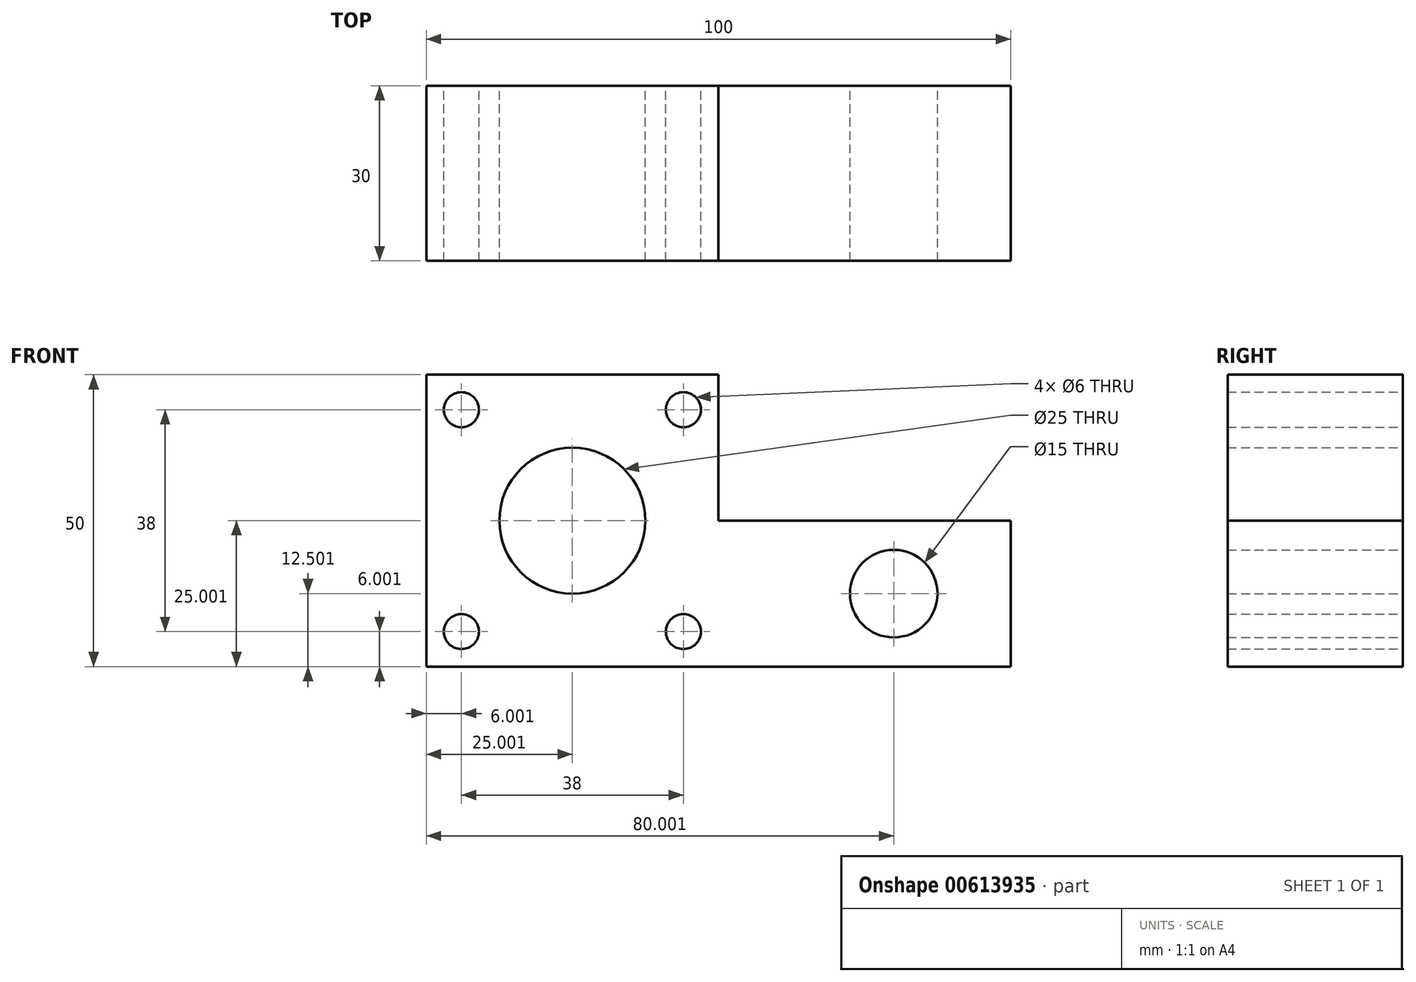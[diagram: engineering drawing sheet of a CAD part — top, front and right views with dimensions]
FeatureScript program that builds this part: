
annotation { "Feature Type Name" : "Feature", "Feature Type Description" : "" }
export const myFeature = defineFeature(function(context is Context, id is Id, definition is map)
    precondition{}
    {
        {
            var Q0;
            Q0=qCreatedBy(makeId("Front.planeOp"),FACE);
            var sketch = newSketch(context, id + "F0", { "sketchPlane" : qUnion([Q0])});
            skLineSegment(sketch, "E0", {"start": v(-45.6, 26.84) * mm, "end": v(-45.6, -23.16) * mm});
            skLineSegment(sketch, "E1", {"start": v(-45.6, -23.16) * mm, "end": v(54.4, -23.16) * mm});
            skLineSegment(sketch, "E2", {"start": v(54.4, -23.16) * mm, "end": v(54.4, 1.84) * mm});
            skLineSegment(sketch, "E3", {"start": v(54.4, 1.84) * mm, "end": v(4.4, 1.84) * mm});
            skLineSegment(sketch, "E4", {"start": v(4.4, 1.84) * mm, "end": v(4.4, 26.84) * mm});
            skLineSegment(sketch, "E5", {"start": v(4.4, 26.84) * mm, "end": v(-45.6, 26.84) * mm});
            skCircle(sketch, "E6", {"center": v(-20.6, 1.84) * mm, "radius": 12.5 * mm});
            skCircle(sketch, "E7", {"center": v(34.4, -10.66) * mm, "radius": 7.5 * mm});
            skCircle(sketch, "E8", {"center": v(-39.6, 20.84) * mm, "radius": 3 * mm});
            skCircle(sketch, "E9", {"center": v(-1.6, 20.84) * mm, "radius": 3 * mm});
            skCircle(sketch, "E10", {"center": v(-1.6, -17.16) * mm, "radius": 3 * mm});
            skCircle(sketch, "E11", {"center": v(-39.6, -17.16) * mm, "radius": 3 * mm});
            skPoint(sketch, "E12.orphan", {"position": v(-20.6, 26.84) * mm});
            skPoint(sketch, "E13.trimOffspring.end.orphan", {"position": v(-45.6, 1.84) * mm});
            skPoint(sketch, "E14.trimOffspring.end.orphan", {"position": v(-1.6, -23.16) * mm});
            skPoint(sketch, "E15.trimOffspring.end.orphan", {"position": v(-39.6, -23.16) * mm});
            skPoint(sketch, "E16.orphan", {"position": v(34.4, -23.16) * mm});
            skPoint(sketch, "E17.start.orphan", {"position": v(54.4, -10.66) * mm});
            skPoint(sketch, "E18.start.orphan", {"position": v(34.4, 1.84) * mm});
            skSolve(sketch);
        }
        {
            var Q0;
            Q0=makeQuery(id+"F0.imprint","IMPRINT",FACE,{"disambiguationData":[TD([[makeQuery(id+"F0.imprint","IMPRINT",EDGE,{"derivedFrom":sQuery(id+"F0.wireOp",EDGE,"E0")}),1.0]])]});
            extrude(context, id + "F1", {"entities" : qUnion([Q0]), "depth" : 30 * mm, "offsetDistance" : 25 * mm});
        }
    });
